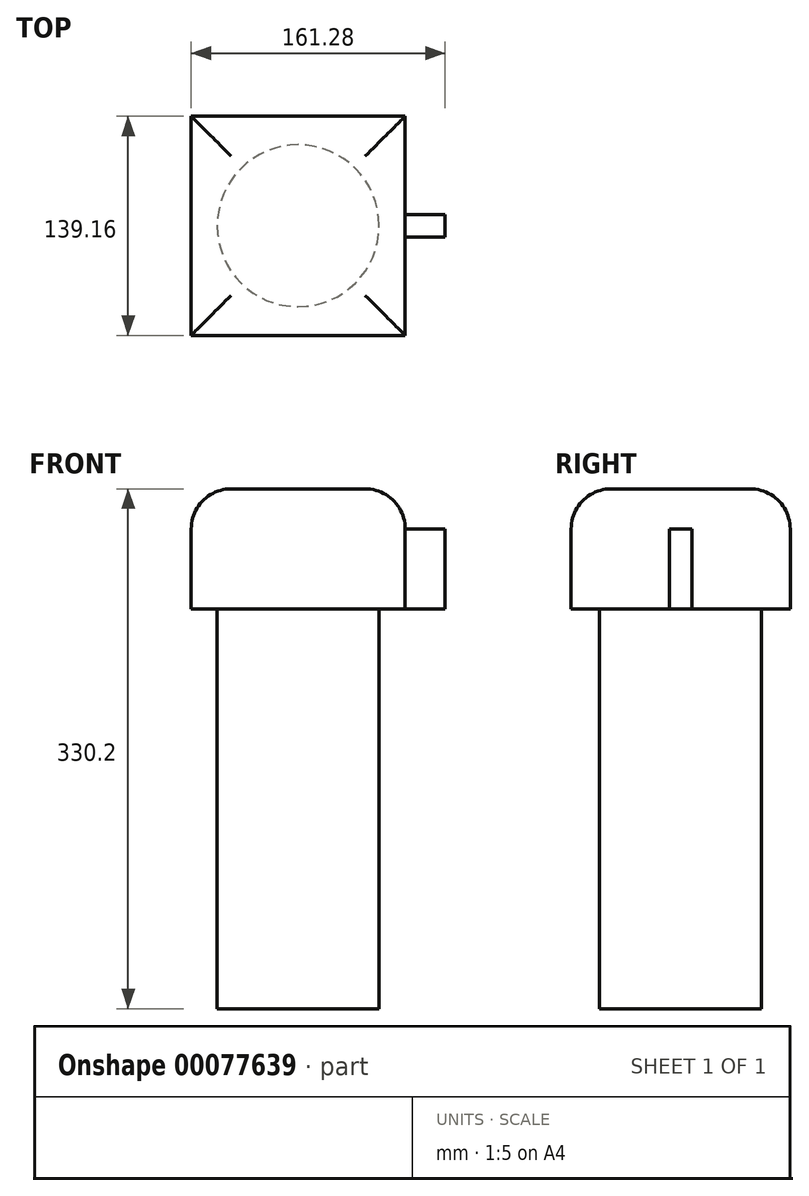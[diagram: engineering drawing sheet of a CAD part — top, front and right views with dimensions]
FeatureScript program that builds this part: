
annotation { "Feature Type Name" : "Feature", "Feature Type Description" : "" }
export const myFeature = defineFeature(function(context is Context, id is Id, definition is map)
    precondition{}
    {
        {
            var Q0;
            Q0=qCreatedBy(makeId("Top.planeOp"),FACE);
            var sketch = newSketch(context, id + "F0", { "sketchPlane" : qUnion([Q0])});
            skCircle(sketch, "E0", {"center": v(0, 0) * mm, "radius": 51.43 * mm});
            skSolve(sketch);
        }
        {
            var Q0;
            Q0 = qSketchRegion(id + "F0", true);
            extrude(context, id + "F1", {"entities" : qUnion([Q0]), "depth" : 254 * mm});
        }
        {
            var Q0;
            Q0=makeQuery(id+"F1.opExtrude","CAP_FACE",FACE,{"disambiguationData":[OSD([sQuery(id+"F0.wireOp",EDGE,"E0")])],"isStart":false});
            var sketch = newSketch(context, id + "F2", { "sketchPlane" : qUnion([Q0])});
            skLineSegment(sketch, "E1.bottom", {"start": v(67.94, 69.58) * mm, "end": v(-67.94, 69.58) * mm});
            skLineSegment(sketch, "E1.top", {"start": v(67.94, -69.58) * mm, "end": v(-67.94, -69.58) * mm});
            skLineSegment(sketch, "E1.left", {"start": v(67.94, 69.58) * mm, "end": v(67.94, -69.58) * mm});
            skLineSegment(sketch, "E1.right", {"start": v(-67.94, 69.58) * mm, "end": v(-67.94, -69.58) * mm});
            skPoint(sketch, "E1.middle", {"position": v(0, 0) * mm});
            skSolve(sketch);
        }
        {
            var Q0;
            Q0 = qSketchRegion(id + "F2", true);
            extrude(context, id + "F3", {"entities" : qUnion([Q0]), "operationType" : NewBodyOperationType.ADD, "depth" : 76.2 * mm});
        }
        {
            var Q0;
            Q0=makeQuery(id+"F3.opExtrude","CAP_EDGE",EDGE,{"disambiguationData":[OSD([sQuery(id+"F2.wireOp",EDGE,"E1.left")])],"isStart":false});
            var Q1;
            Q1=makeQuery(id+"F3.opExtrude","CAP_EDGE",EDGE,{"disambiguationData":[OSD([sQuery(id+"F2.wireOp",EDGE,"E1.bottom")])],"isStart":false});
            var Q2;
            Q2=makeQuery(id+"F3.opExtrude","CAP_EDGE",EDGE,{"disambiguationData":[OSD([sQuery(id+"F2.wireOp",EDGE,"E1.right")])],"isStart":false});
            var Q3;
            Q3=makeQuery(id+"F3.opExtrude","CAP_EDGE",EDGE,{"disambiguationData":[OSD([sQuery(id+"F2.wireOp",EDGE,"E1.top")])],"isStart":false});
            fillet(context, id + "F4", {"entities" : qUnion([Q0, Q1, Q2, Q3]), "radius" : 25.4 * mm, "tangentPropagation" : true, "allowEdgeOverflow" : false});
        }
        {
            var Q0;
            Q0=makeQuery(id+"F3.opExtrude","SWEPT_FACE",FACE,{"disambiguationData":[OSD([sQuery(id+"F2.wireOp",EDGE,"E1.left")])]});
            var sketch = newSketch(context, id + "F5", { "sketchPlane" : qUnion([Q0])});
            skLineSegment(sketch, "E2.bottom", {"start": v(7.15, 304.8) * mm, "end": v(-7.15, 304.8) * mm});
            skLineSegment(sketch, "E2.top", {"start": v(7.15, 251.96) * mm, "end": v(-7.15, 251.96) * mm});
            skLineSegment(sketch, "E2.left", {"start": v(7.15, 304.8) * mm, "end": v(7.15, 251.96) * mm});
            skLineSegment(sketch, "E2.right", {"start": v(-7.15, 304.8) * mm, "end": v(-7.15, 251.96) * mm});
            skPoint(sketch, "E2.middle", {"position": v(0, 278.38) * mm});
            skSolve(sketch);
        }
        {
            var Q0;
            {var subQ0=sQuery(id+"F5.wireOp",EDGE,"E2.bottom");Q0=makeQuery(id+"F5.imprint","IMPRINT",FACE,{"disambiguationData":[TD([[makeQuery(id+"F5.imprint","IMPRINT",EDGE,{"derivedFrom":subQ0}),1.0]])]});}
            extrude(context, id + "F6", {"entities" : qUnion([Q0]), "operationType" : NewBodyOperationType.ADD, "depth" : 25.4 * mm});
        }
    });
